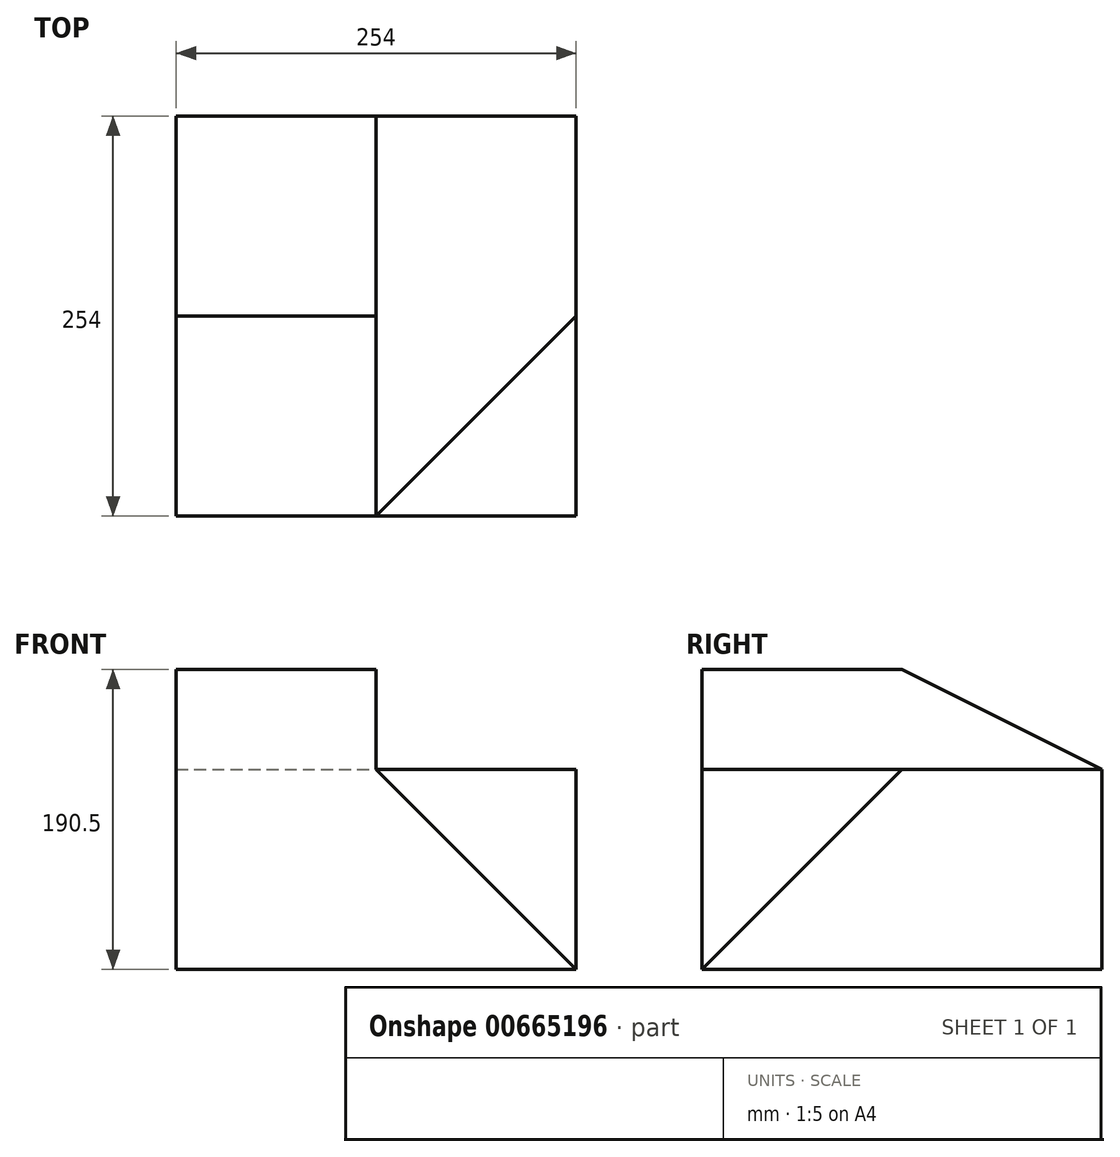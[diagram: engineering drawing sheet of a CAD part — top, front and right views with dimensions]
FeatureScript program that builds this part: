
annotation { "Feature Type Name" : "Feature", "Feature Type Description" : "" }
export const myFeature = defineFeature(function(context is Context, id is Id, definition is map)
    precondition{}
    {
        {
            var Q0;
            Q0=qCreatedBy(makeId("Top.planeOp"),FACE);
            var sketch = newSketch(context, id + "F0", { "sketchPlane" : qUnion([Q0])});
            skLineSegment(sketch, "E0", {"start": v(0, 0) * mm, "end": v(0, 254) * mm});
            skLineSegment(sketch, "E1", {"start": v(0, 254) * mm, "end": v(254, 254) * mm});
            skLineSegment(sketch, "E2", {"start": v(254, 254) * mm, "end": v(254, 0) * mm});
            skLineSegment(sketch, "E3", {"start": v(254, 0) * mm, "end": v(0, 0) * mm});
            skSolve(sketch);
        }
        {
            var Q0;
            Q0=makeQuery(id+"F0.imprint","IMPRINT",FACE,{"disambiguationData":[TD([[makeQuery(id+"F0.imprint","IMPRINT",EDGE,{"derivedFrom":sQuery(id+"F0.wireOp",EDGE,"E0")}),-1.0]])]});
            extrude(context, id + "F1", {"entities" : qUnion([Q0]), "endBound" : BoundingType.SYMMETRIC, "depth" : 127 * mm, "offsetDistance" : 25.4 * mm});
        }
        {
            var Q0;
            Q0=makeQuery(id+"F1.opExtrude","SWEPT_FACE",FACE,{"disambiguationData":[OSD([sQuery(id+"F0.wireOp",EDGE,"E0")])]});
            var sketch = newSketch(context, id + "F2", { "sketchPlane" : qUnion([Q0])});
            skLineSegment(sketch, "E4", {"start": v(0, 63.5) * mm, "end": v(0, 127) * mm});
            skLineSegment(sketch, "E5", {"start": v(0, 127) * mm, "end": v(-127, 127) * mm});
            skLineSegment(sketch, "E6", {"start": v(-127, 127) * mm, "end": v(-127, 63.5) * mm});
            skLineSegment(sketch, "E7", {"start": v(-254, 63.5) * mm, "end": v(-127, 127) * mm});
            skSolve(sketch);
        }
        {
            var Q0;
            {var subQ0=sQuery(id+"F2.wireOp",EDGE,"E4");Q0=makeQuery(id+"F2.imprint","IMPRINT",FACE,{"disambiguationData":[TD([[makeQuery(id+"F2.imprint","IMPRINT",EDGE,{"derivedFrom":subQ0}),1.0]])]});}
            var Q1;
            {var subQ0=sQuery(id+"F2.wireOp",EDGE,"E6");Q1=makeQuery(id+"F2.imprint","IMPRINT",FACE,{"disambiguationData":[TD([[makeQuery(id+"F2.imprint","IMPRINT",EDGE,{"derivedFrom":subQ0}),-1.0]])]});}
            extrude(context, id + "F3", {"entities" : qUnion([Q0, Q1]), "operationType" : NewBodyOperationType.ADD, "oppositeDirection" : true, "depth" : 127 * mm, "offsetDistance" : 25.4 * mm});
        }
        {
            var Q0;
            Q0=makeQuery(id+"F1.opExtrude","CAP_FACE",FACE,{"disambiguationData":[OSD([sQuery(id+"F0.wireOp",EDGE,"E0"),sQuery(id+"F0.wireOp",EDGE,"E1"),sQuery(id+"F0.wireOp",EDGE,"E2"),sQuery(id+"F0.wireOp",EDGE,"E3")])],"isStart":false});
            var sketch = newSketch(context, id + "F4", { "sketchPlane" : qUnion([Q0])});
            skPoint(sketch, "E8", {"position": v(127, 0) * mm});
            skPoint(sketch, "E9", {"position": v(254, 127) * mm});
            skSolve(sketch);
        }
        {
            var Q0;
            Q0=makeQuery(id+"F3.boolean.opBoolean","MERGE",FACE,{"derivedFrom":[makeQuery(id+"F1.opExtrude","SWEPT_FACE",FACE,{"disambiguationData":[OSD([sQuery(id+"F0.wireOp",EDGE,"E3")])]}),makeQuery(id+"F3.opExtrude","SWEPT_FACE",FACE,{"disambiguationData":[OSD([sQuery(id+"F2.wireOp",EDGE,"E4")])]})]});
            var sketch = newSketch(context, id + "F5", { "sketchPlane" : qUnion([Q0])});
            skPoint(sketch, "E10", {"position": v(254, -63.5) * mm});
            skSolve(sketch);
        }
        {
            var Q0;
            Q0=sQuery(id+"F4.wireOp",VERTEX,"E8");
            var Q1;
            Q1=sQuery(id+"F4.wireOp",VERTEX,"E9");
            var Q2;
            Q2=sQuery(id+"F5.wireOp",VERTEX,"E10");
            cPlane(context, id + "F6", {"entities" : qUnion([Q0, Q1, Q2]), "cplaneType" : CPlaneType.THREE_POINT, "offset" : 25.4 * mm, "width" : 152.4 * mm, "height" : 152.4 * mm});
        }
        {
            var Q0;
            Q0=qCreatedBy(id+"F6.planeOp",FACE);
            var sketch = newSketch(context, id + "F7", { "sketchPlane" : qUnion([Q0])});
            skLineSegment(sketch, "E11", {"start": v(77.77, 44.9) * mm, "end": v(233.31, 134.7) * mm});
            skLineSegment(sketch, "E12", {"start": v(77.77, 44.9) * mm, "end": v(233.31, -44.9) * mm});
            skLineSegment(sketch, "E13", {"start": v(233.31, -44.9) * mm, "end": v(233.31, 134.7) * mm});
            skSolve(sketch);
        }
        {
            var Q0;
            Q0 = qSketchRegion(id + "F7", true);
            extrude(context, id + "F8", {"entities" : qUnion([Q0]), "operationType" : NewBodyOperationType.REMOVE, "endBound" : BoundingType.THROUGH_ALL, "depth" : 25.4 * mm, "offsetDistance" : 25.4 * mm});
        }
    });
